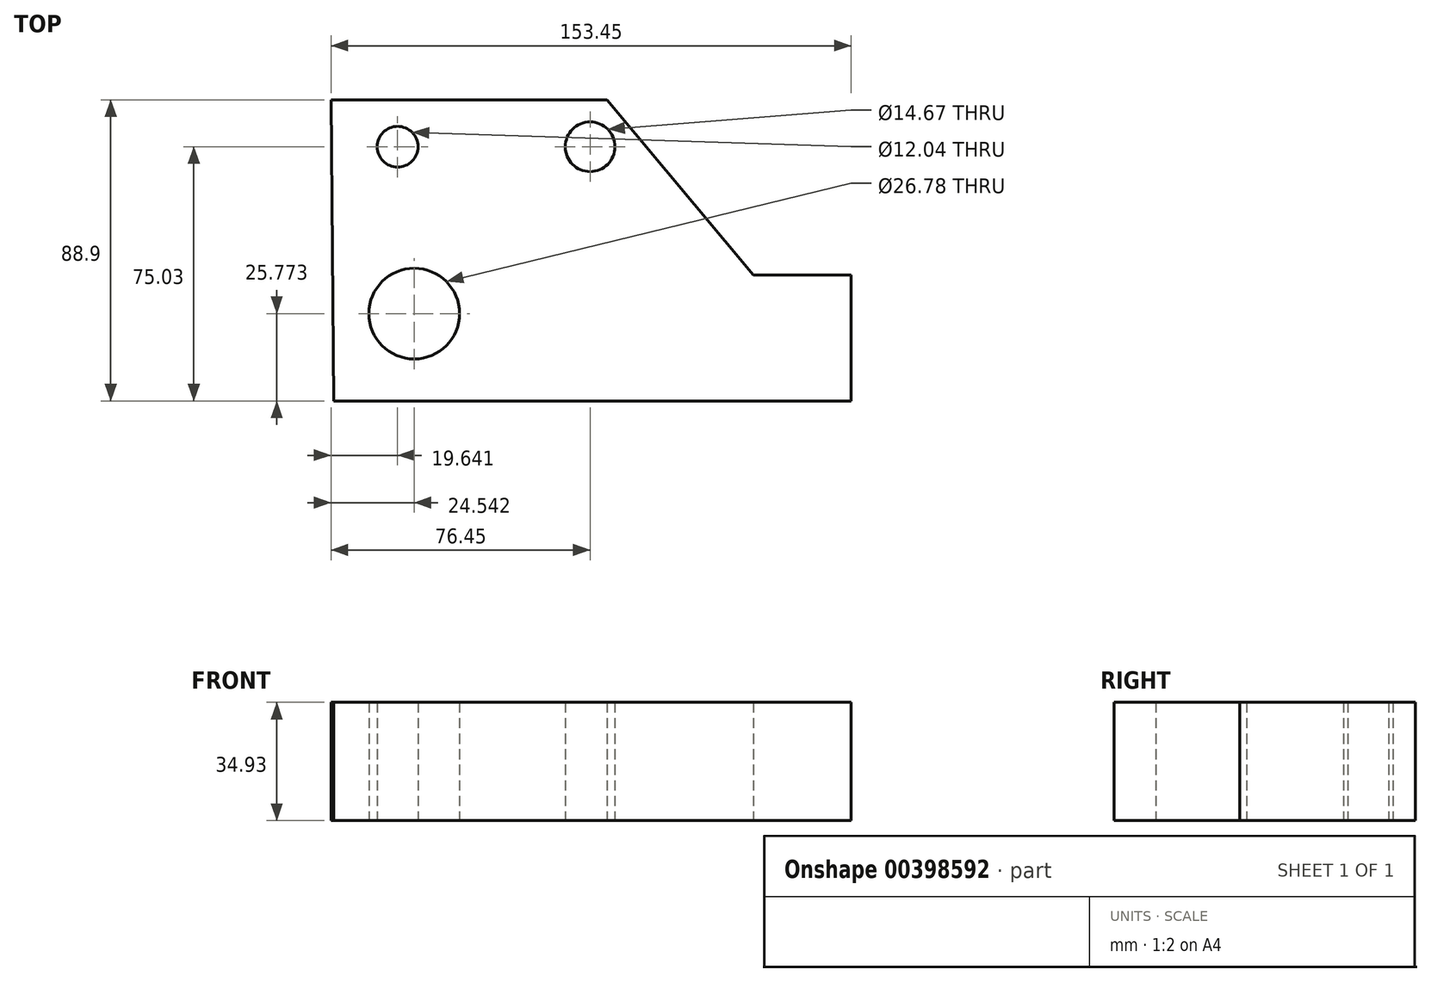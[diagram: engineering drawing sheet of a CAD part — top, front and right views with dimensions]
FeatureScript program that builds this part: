
annotation { "Feature Type Name" : "Feature", "Feature Type Description" : "" }
export const myFeature = defineFeature(function(context is Context, id is Id, definition is map)
    precondition{}
    {
        {
            var Q0;
            Q0=qCreatedBy(makeId("Top.planeOp"),FACE);
            var sketch = newSketch(context, id + "F0", { "sketchPlane" : qUnion([Q0])});
            skLineSegment(sketch, "E0", {"start": v(-75.6, -75.03) * mm, "end": v(77, -75.03) * mm});
            skLineSegment(sketch, "E1", {"start": v(77, -75.03) * mm, "end": v(77, -37.88) * mm});
            skLineSegment(sketch, "E2", {"start": v(77, -37.88) * mm, "end": v(48.17, -37.88) * mm});
            skLineSegment(sketch, "E3", {"start": v(48.17, -37.88) * mm, "end": v(5.04, 13.87) * mm});
            skLineSegment(sketch, "E4", {"start": v(5.04, 13.87) * mm, "end": v(-76.45, 13.87) * mm});
            skLineSegment(sketch, "E5", {"start": v(-76.45, 13.87) * mm, "end": v(-75.6, -75.03) * mm});
            skCircle(sketch, "E6", {"center": v(0, 0) * mm, "radius": 7.33 * mm});
            skCircle(sketch, "E7", {"center": v(-56.8, 0) * mm, "radius": 6.02 * mm});
            skCircle(sketch, "E8", {"center": v(-51.9, -49.26) * mm, "radius": 13.39 * mm});
            skSolve(sketch);
        }
        {
            var Q0;
            Q0 = qSketchRegion(id + "F0", true);
            extrude(context, id + "F1", {"entities" : qUnion([Q0]), "depth" : 9.52 * mm});
        }
        {
            var Q0;
            Q0=makeQuery(id+"F1.opExtrude","CAP_FACE",FACE,{"disambiguationData":[OSD([sQuery(id+"F0.wireOp",EDGE,"E0"),sQuery(id+"F0.wireOp",EDGE,"E1"),sQuery(id+"F0.wireOp",EDGE,"E2"),sQuery(id+"F0.wireOp",EDGE,"E3"),sQuery(id+"F0.wireOp",EDGE,"E4"),sQuery(id+"F0.wireOp",EDGE,"E5"),sQuery(id+"F0.wireOp",EDGE,"E6"),sQuery(id+"F0.wireOp",EDGE,"E7"),sQuery(id+"F0.wireOp",EDGE,"E8")])],"isStart":false});
            extrude(context, id + "F2", {"entities" : qUnion([Q0]), "operationType" : NewBodyOperationType.ADD, "depth" : 25.4 * mm});
        }
    });
